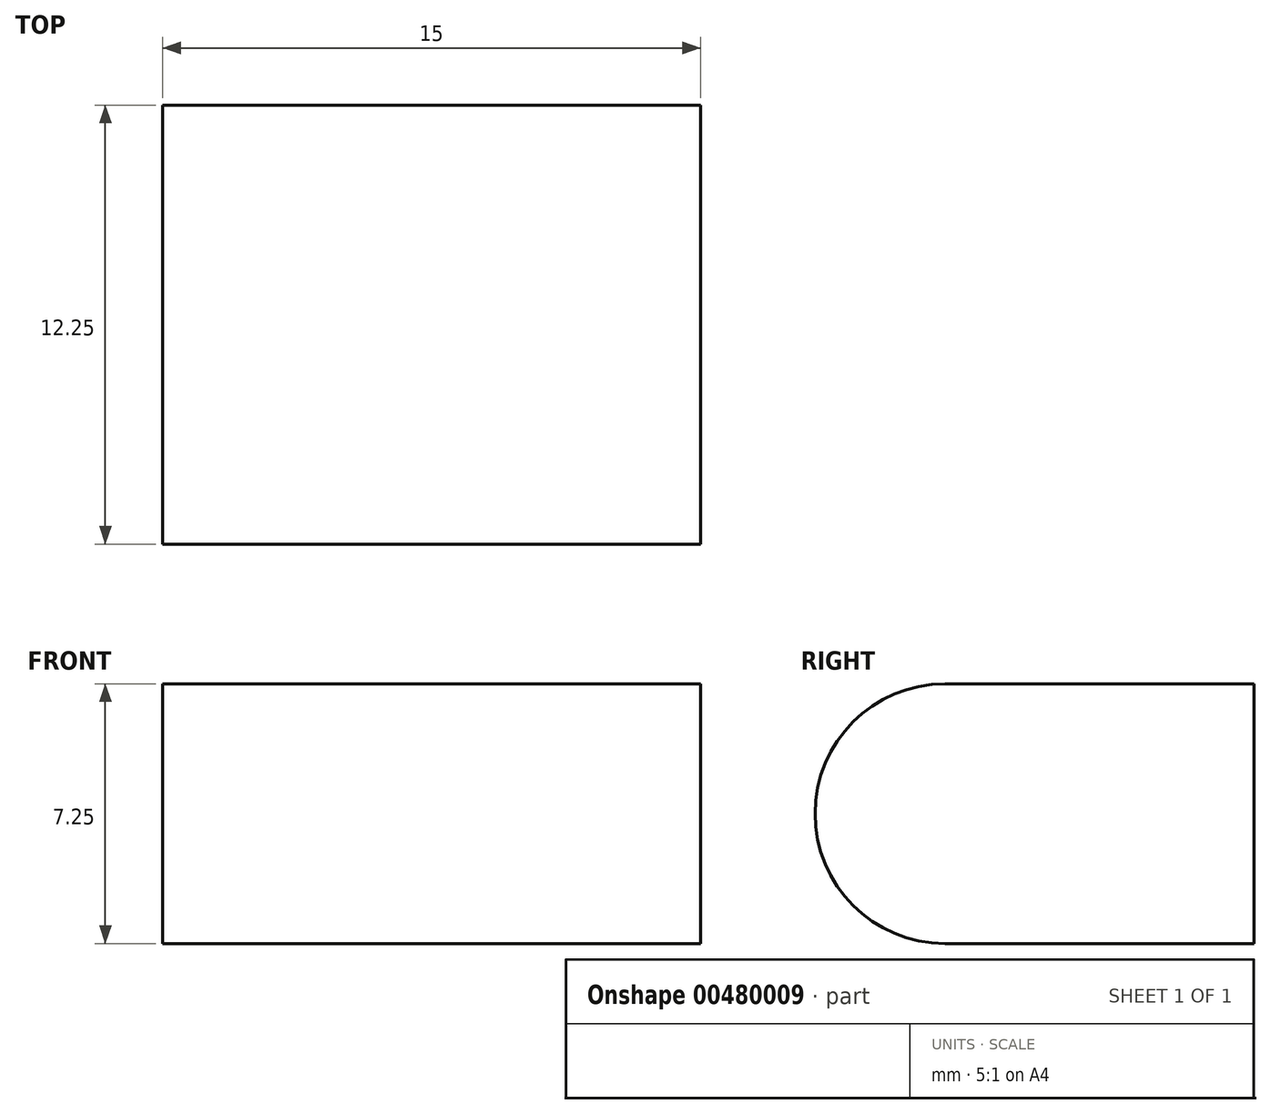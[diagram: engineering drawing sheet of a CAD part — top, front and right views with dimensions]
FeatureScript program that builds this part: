
annotation { "Feature Type Name" : "Feature", "Feature Type Description" : "" }
export const myFeature = defineFeature(function(context is Context, id is Id, definition is map)
    precondition{}
    {
        {
            var Q0;
            Q0=qCreatedBy(makeId("Front.planeOp"),FACE);
            var sketch = newSketch(context, id + "F0", { "sketchPlane" : qUnion([Q0])});
            skLineSegment(sketch, "E0.0.0", {"start": v(-69.66, 36.6) * mm, "end": v(-54.66, 36.6) * mm});
            skLineSegment(sketch, "E0.0.1", {"start": v(-54.66, 36.6) * mm, "end": v(-54.66, 43.85) * mm});
            skLineSegment(sketch, "E0.0.2", {"start": v(-54.66, 43.85) * mm, "end": v(-69.66, 43.85) * mm});
            skLineSegment(sketch, "E0.0.3", {"start": v(-69.66, 43.85) * mm, "end": v(-69.66, 36.6) * mm});
            skSolve(sketch);
        }
        {
            var Q0;
            Q0=makeQuery(id+"F0.imprint","IMPRINT",FACE,{"disambiguationData":[TD([[makeQuery(id+"F0.imprint","IMPRINT",EDGE,{"derivedFrom":sQuery(id+"F0.wireOp",EDGE,"E0.0.0")}),1.0]])]});
            extrude(context, id + "F1", {"entities" : qUnion([Q0]), "depth" : 8.62 * mm});
        }
        {
            var Q0;
            Q0=makeQuery(id+"F1.opExtrude","SWEPT_FACE",FACE,{"disambiguationData":[OSD([sQuery(id+"F0.wireOp",EDGE,"E0.0.1")])]});
            var sketch = newSketch(context, id + "F2", { "sketchPlane" : qUnion([Q0])});
            skArc(sketch, "E1", {"start": v(-8.62, 43.85) * mm, "mid": v(-12.25, 40.22) * mm, "end": v(-8.62, 36.6) * mm});
            skSolve(sketch);
        }
        {
            var Q0;
            Q0=makeQuery(id+"F2.imprint","IMPRINT",FACE,{"disambiguationData":[TD([[makeQuery(id+"F2.imprint","IMPRINT",EDGE,{"derivedFrom":sQuery(id+"F2.wireOp",EDGE,"E1")}),1.0]])]});
            var Q1;
            Q1=sQuery(id+"F2.wireOp",EDGE,"E1");
            extrude(context, id + "F3", {"entities" : qUnion([Q0]), "operationType" : NewBodyOperationType.ADD, "surfaceEntities" : qUnion([Q1]), "oppositeDirection" : true, "depth" : 15 * mm});
        }
    });
